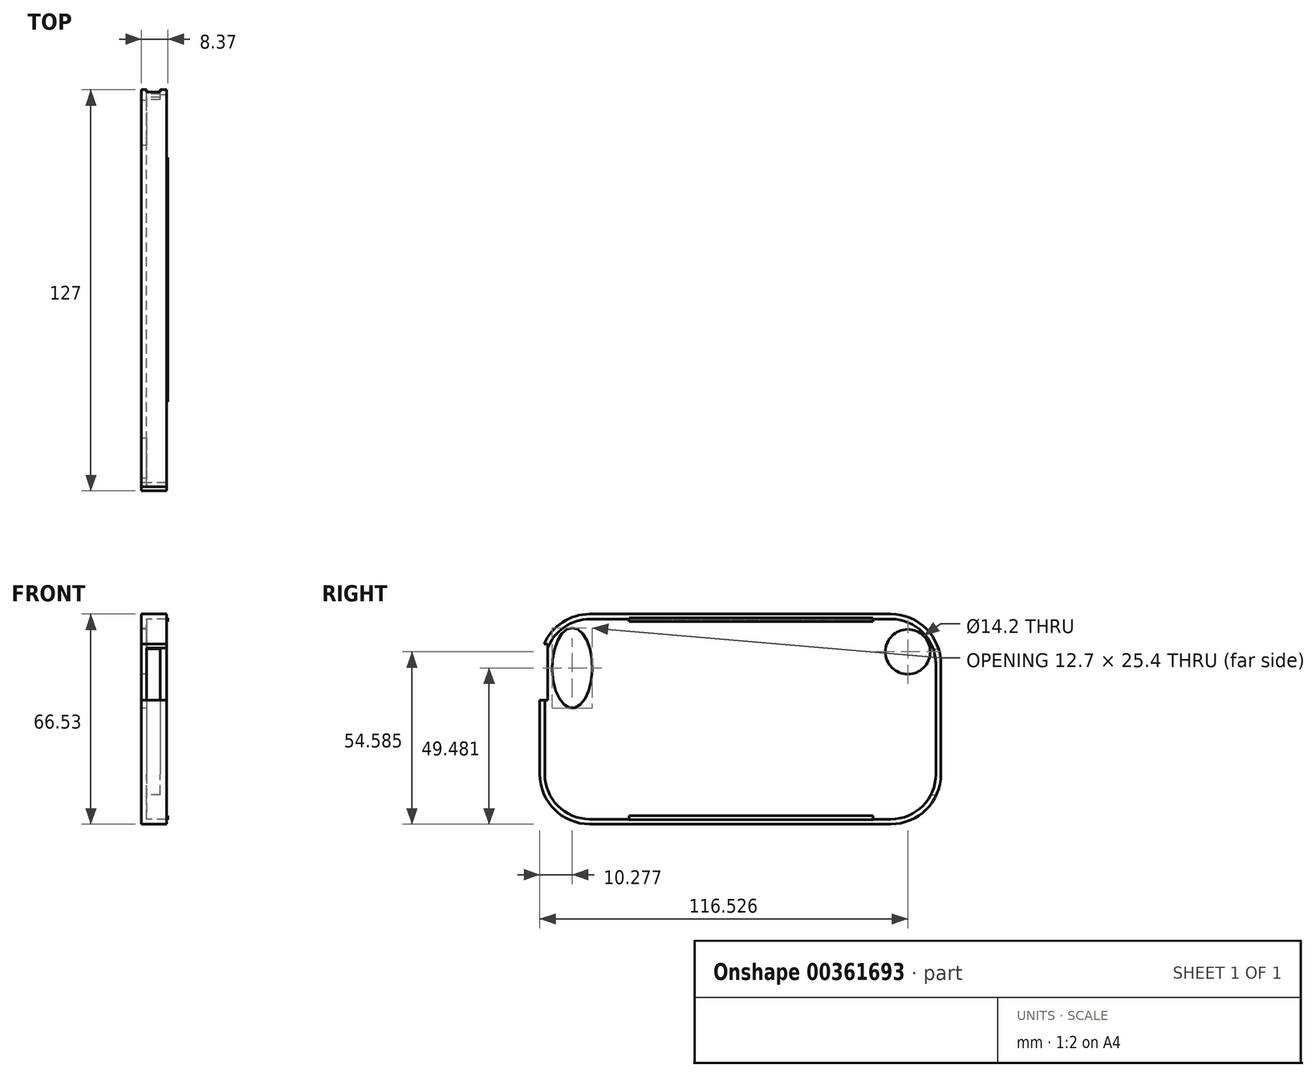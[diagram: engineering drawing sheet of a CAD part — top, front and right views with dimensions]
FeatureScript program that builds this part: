
annotation { "Feature Type Name" : "Feature", "Feature Type Description" : "" }
export const myFeature = defineFeature(function(context is Context, id is Id, definition is map)
    precondition{}
    {
        {
            var Q0;
            Q0=qCreatedBy(makeId("Right.planeOp"),FACE);
            var sketch = newSketch(context, id + "F0", { "sketchPlane" : qUnion([Q0])});
            skLineSegment(sketch, "E0", {"start": v(-37.83, 63.5) * mm, "end": v(57.42, 63.5) * mm});
            skLineSegment(sketch, "E1", {"start": v(-37.83, 0.15) * mm, "end": v(57.42, 0.15) * mm});
            skLineSegment(sketch, "E2", {"start": v(-52.12, 49.21) * mm, "end": v(-52.12, 14.44) * mm});
            skLineSegment(sketch, "E3", {"start": v(71.7, 49.21) * mm, "end": v(71.7, 14.44) * mm});
            skPoint(sketch, "E4.visualSharp", {"position": v(-52.12, 63.5) * mm});
            skArc(sketch, "E4.filletArc", {"start": v(-37.83, 63.5) * mm, "mid": v(-47.94, 59.32) * mm, "end": v(-52.12, 49.21) * mm});
            skPoint(sketch, "E5.visualSharp", {"position": v(71.7, 63.5) * mm});
            skArc(sketch, "E5.filletArc", {"start": v(71.7, 49.21) * mm, "mid": v(67.52, 59.32) * mm, "end": v(57.42, 63.5) * mm});
            skPoint(sketch, "E6.newPointA", {"position": v(-52.12, 0) * mm});
            skPoint(sketch, "E6.newPointB", {"position": v(-52.12, 0.15) * mm});
            skArc(sketch, "E6.filletArc", {"start": v(-52.12, 14.44) * mm, "mid": v(-47.94, 4.34) * mm, "end": v(-37.83, 0.15) * mm});
            skPoint(sketch, "E7.newPointA", {"position": v(71.7, 0) * mm});
            skPoint(sketch, "E7.newPointB", {"position": v(71.7, 0.15) * mm});
            skArc(sketch, "E7.filletArc", {"start": v(57.42, 0.15) * mm, "mid": v(67.52, 4.34) * mm, "end": v(71.7, 14.44) * mm});
            skSolve(sketch);
        }
        {
            var Q0;
            Q0=makeQuery(id+"F0.imprint","IMPRINT",FACE,{"disambiguationData":[TD([[makeQuery(id+"F0.imprint","IMPRINT",EDGE,{"derivedFrom":sQuery(id+"F0.wireOp",EDGE,"E0")}),-1.0]])]});
            extrude(context, id + "F1", {"entities" : qUnion([Q0]), "depth" : 6.35 * mm});
        }
        {
            var Q0;
            Q0=makeQuery(id+"F1.opExtrude","CAP_FACE",FACE,{"disambiguationData":[OSD([sQuery(id+"F0.wireOp",EDGE,"E0"),sQuery(id+"F0.wireOp",EDGE,"E1"),sQuery(id+"F0.wireOp",EDGE,"E2"),sQuery(id+"F0.wireOp",EDGE,"E3"),sQuery(id+"F0.wireOp",EDGE,"E4.filletArc"),sQuery(id+"F0.wireOp",EDGE,"E5.filletArc"),sQuery(id+"F0.wireOp",EDGE,"E6.filletArc"),sQuery(id+"F0.wireOp",EDGE,"E7.filletArc")])],"isStart":false});
            shell(context, id + "F2", {"entities" : qUnion([Q0]), "thickness" : 1.59 * mm, "oppositeDirection" : true});
        }
        {
            var Q0;
            Q0=qCreatedBy(makeId("Right.planeOp"),FACE);
            var sketch = newSketch(context, id + "F3", { "sketchPlane" : qUnion([Q0])});
            skEllipse(sketch, "E8", {"center": v(-43.43, 48.04) * mm, "majorRadius": 12.7 * mm, "minorRadius": 6.35 * mm, "majorAxis": v(0, 1)});
            skSolve(sketch);
        }
        {
            var Q0;
            Q0 = qSketchRegion(id + "F3", true);
            extrude(context, id + "F4", {"entities" : qUnion([Q0]), "operationType" : NewBodyOperationType.REMOVE, "oppositeDirection" : true, "depth" : 25.4 * mm});
        }
        {
            var Q0;
            Q0=qCreatedBy(makeId("Right.planeOp"),FACE);
            cPlane(context, id + "F5", {"entities" : qUnion([Q0]), "cplaneType" : CPlaneType.OFFSET, "offset" : 6.35 * mm, "width" : 152.4 * mm, "height" : 152.4 * mm});
        }
        {
            var Q0;
            Q0=qCreatedBy(id+"F5.planeOp",FACE);
            var sketch = newSketch(context, id + "F6", { "sketchPlane" : qUnion([Q0])});
            skLineSegment(sketch, "E9", {"start": v(482.7, 3.17) * mm, "end": v(482.7, 0) * mm});
            skLineSegment(sketch, "E10", {"start": v(-25.43, 62.75) * mm, "end": v(51.85, 62.75) * mm});
            skLineSegment(sketch, "E11", {"start": v(51.85, 62.75) * mm, "end": v(51.85, 63.85) * mm});
            skLineSegment(sketch, "E12", {"start": v(51.85, 63.85) * mm, "end": v(-25.43, 63.85) * mm});
            skLineSegment(sketch, "E13", {"start": v(-25.43, 63.85) * mm, "end": v(-25.43, 62.75) * mm});
            skLineSegment(sketch, "E14", {"start": v(-25.43, 1.27) * mm, "end": v(51.85, 1.27) * mm});
            skLineSegment(sketch, "E15", {"start": v(51.85, 1.27) * mm, "end": v(51.85, 0) * mm});
            skLineSegment(sketch, "E16", {"start": v(51.85, 0) * mm, "end": v(-25.43, 0) * mm});
            skLineSegment(sketch, "E17", {"start": v(-25.43, 0) * mm, "end": v(-25.43, 1.27) * mm});
            skSolve(sketch);
        }
        {
            var Q0;
            Q0=makeQuery(id+"F6.imprint","IMPRINT",FACE,{"disambiguationData":[TD([[makeQuery(id+"F6.imprint","IMPRINT",EDGE,{"derivedFrom":sQuery(id+"F6.wireOp",EDGE,"E14")}),-1.0]])]});
            var Q1;
            Q1=makeQuery(id+"F6.imprint","IMPRINT",FACE,{"disambiguationData":[TD([[makeQuery(id+"F6.imprint","IMPRINT",EDGE,{"derivedFrom":sQuery(id+"F6.wireOp",EDGE,"E10")}),1.0]])]});
            extrude(context, id + "F7", {"entities" : qUnion([Q0, Q1]), "operationType" : NewBodyOperationType.ADD, "depth" : 0.43 * mm});
        }
        {
            var Q0;
            Q0=makeQuery(id+"F1.opExtrude","CAP_FACE",FACE,{"disambiguationData":[OSD([sQuery(id+"F0.wireOp",EDGE,"E0"),sQuery(id+"F0.wireOp",EDGE,"E1"),sQuery(id+"F0.wireOp",EDGE,"E2"),sQuery(id+"F0.wireOp",EDGE,"E3"),sQuery(id+"F0.wireOp",EDGE,"E4.filletArc"),sQuery(id+"F0.wireOp",EDGE,"E5.filletArc"),sQuery(id+"F0.wireOp",EDGE,"E6.filletArc"),sQuery(id+"F0.wireOp",EDGE,"E7.filletArc")])],"isStart":true});
            var sketch = newSketch(context, id + "F8", { "sketchPlane" : qUnion([Q0])});
            skCircle(sketch, "E18", {"center": v(-62.82, 53.15) * mm, "radius": 7.1 * mm});
            skSolve(sketch);
        }
        {
            var Q0;
            Q0=makeQuery(id+"F8.imprint","IMPRINT",FACE,{"disambiguationData":[TD([[makeQuery(id+"F8.imprint","IMPRINT",EDGE,{"derivedFrom":sQuery(id+"F8.wireOp",EDGE,"E18")}),1.0]])]});
            extrude(context, id + "F9", {"entities" : qUnion([Q0]), "operationType" : NewBodyOperationType.REMOVE, "oppositeDirection" : true, "depth" : 0.25 * mm, "offsetDistance" : 25.4 * mm});
        }
        {
            var Q0;
            Q0=makeQuery(id+"F9.boolean.opBoolean","COPY",FACE,{"derivedFrom":makeQuery(id+"F9.opExtrude","CAP_FACE",FACE,{"disambiguationData":[OSD([sQuery(id+"F8.wireOp",EDGE,"E18")])],"isStart":false})});
            extrude(context, id + "F10", {"entities" : qUnion([Q0]), "operationType" : NewBodyOperationType.REMOVE, "oppositeDirection" : true, "depth" : 1.42 * mm, "offsetDistance" : 25.4 * mm});
        }
        {
            var Q0;
            Q0=makeQuery(id+"F1.opExtrude","SWEPT_FACE",FACE,{"disambiguationData":[OSD([sQuery(id+"F0.wireOp",EDGE,"E2")])]});
            var sketch = newSketch(context, id + "F11", { "sketchPlane" : qUnion([Q0])});
            skLineSegment(sketch, "E19.bottom", {"start": v(6.35, 55.6) * mm, "end": v(-1.59, 55.6) * mm});
            skLineSegment(sketch, "E19.top", {"start": v(6.35, 37.82) * mm, "end": v(-1.59, 37.82) * mm});
            skLineSegment(sketch, "E19.left", {"start": v(6.35, 55.6) * mm, "end": v(6.35, 37.82) * mm});
            skLineSegment(sketch, "E19.right", {"start": v(-1.59, 55.6) * mm, "end": v(-1.59, 37.82) * mm});
            skSolve(sketch);
        }
        {
            var Q0;
            {var subQ0=sQuery(id+"F11.wireOp",EDGE,"E19.bottom");Q0=makeQuery(id+"F11.imprint","IMPRINT",FACE,{"disambiguationData":[TD([[makeQuery(id+"F11.imprint","IMPRINT",EDGE,{"derivedFrom":subQ0}),1.0]])]});}
            var Q1;
            {var subQ0=sQuery(id+"F11.wireOp",EDGE,"E19.top");Q1=makeQuery(id+"F11.imprint","IMPRINT",FACE,{"disambiguationData":[TD([[makeQuery(id+"F11.imprint","IMPRINT",EDGE,{"derivedFrom":subQ0}),-1.0]])]});}
            extrude(context, id + "F12", {"entities" : qUnion([Q0, Q1]), "operationType" : NewBodyOperationType.REMOVE, "oppositeDirection" : true, "depth" : 2.54 * mm, "offsetDistance" : 25.4 * mm});
        }
        {
            var Q0;
            Q0=makeQuery(id+"F1.opExtrude","SWEPT_FACE",FACE,{"disambiguationData":[OSD([sQuery(id+"F0.wireOp",EDGE,"E3")])]});
            var sketch = newSketch(context, id + "F13", { "sketchPlane" : qUnion([Q0])});
            skLineSegment(sketch, "E20.bottom", {"start": v(-4.34, 54.04) * mm, "end": v(0, 54.04) * mm});
            skLineSegment(sketch, "E20.top", {"start": v(-4.34, 7.9) * mm, "end": v(0, 7.9) * mm});
            skLineSegment(sketch, "E20.left", {"start": v(-4.34, 54.04) * mm, "end": v(-4.34, 7.9) * mm});
            skLineSegment(sketch, "E20.right", {"start": v(0, 54.04) * mm, "end": v(0, 7.9) * mm});
            skSolve(sketch);
        }
        {
            var Q0;
            {var subQ0=sQuery(id+"F13.wireOp",EDGE,"E20.left");var subQ1=sQuery(id+"F0.wireOp",EDGE,"E3");var subQ2=makeQuery(id+"F1.opExtrude","SWEPT_EDGE",EDGE,{"disambiguationData":[OSD([subQ1,sQuery(id+"F0.wireOp",EDGE,"E5.filletArc")])]});var subQ3=makeQuery(id+"F13.imprint","INTERSECT",VERTEX,{"derivedFrom":[subQ2,subQ0]});Q0=makeQuery(id+"F13.imprint","IMPRINT",FACE,{"disambiguationData":[TD([[makeQuery(id+"F13.imprint","IMPRINT",EDGE,{"disambiguationData":[TD([[subQ3,-1.0]])],"derivedFrom":subQ0}),1.0]])]});}
            var Q1;
            {var subQ0=sQuery(id+"F13.wireOp",EDGE,"E20.bottom");Q1=makeQuery(id+"F13.imprint","IMPRINT",FACE,{"disambiguationData":[TD([[makeQuery(id+"F13.imprint","IMPRINT",EDGE,{"derivedFrom":subQ0}),-1.0]])]});}
            var Q2;
            {var subQ0=sQuery(id+"F13.wireOp",EDGE,"E20.top");Q2=makeQuery(id+"F13.imprint","IMPRINT",FACE,{"disambiguationData":[TD([[makeQuery(id+"F13.imprint","IMPRINT",EDGE,{"derivedFrom":subQ0}),1.0]])]});}
            extrude(context, id + "F14", {"entities" : qUnion([Q0, Q1, Q2]), "operationType" : NewBodyOperationType.REMOVE, "oppositeDirection" : true, "depth" : 25.4 * mm, "offsetDistance" : 25.4 * mm});
        }
    });
